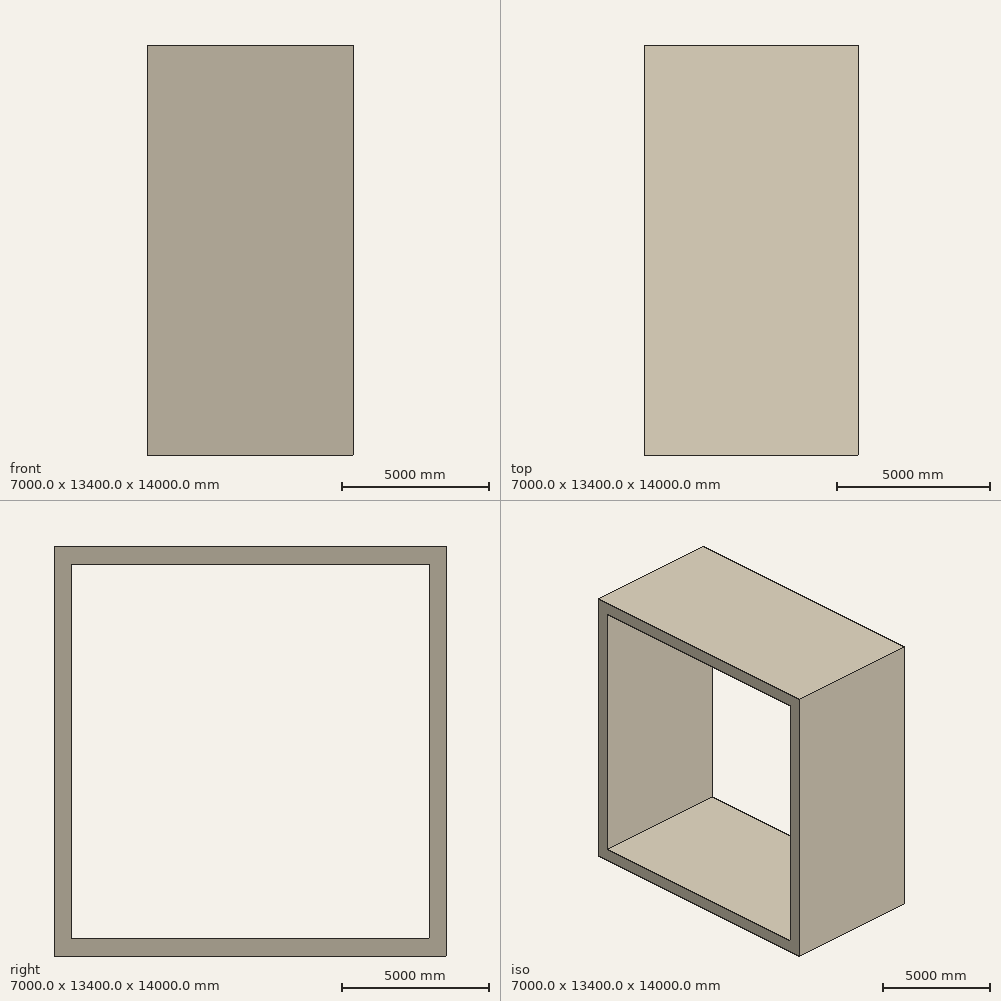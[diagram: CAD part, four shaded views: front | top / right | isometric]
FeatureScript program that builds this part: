
annotation { "Feature Type Name" : "Feature", "Feature Type Description" : "" }
export const myFeature = defineFeature(function(context is Context, id is Id, definition is map)
    precondition{}
    {
        {
            var Q0;
            Q0=qCreatedBy(makeId("Right.planeOp"),FACE);
            var sketch = newSketch(context, id + "F0", { "sketchPlane" : qUnion([Q0])});
            skLineSegment(sketch, "E0.bottom", {"start": v(-6251.52, 6663.35) * mm, "end": v(7148.48, 6663.35) * mm});
            skLineSegment(sketch, "E0.top", {"start": v(-6251.52, -7336.65) * mm, "end": v(7148.48, -7336.65) * mm});
            skLineSegment(sketch, "E0.left", {"start": v(-6251.52, 6663.35) * mm, "end": v(-6251.52, -7336.65) * mm});
            skLineSegment(sketch, "E0.right", {"start": v(7148.48, 6663.35) * mm, "end": v(7148.48, -7336.65) * mm});
            skLineSegment(sketch, "E1.bottom", {"start": v(6548.48, 6063.35) * mm, "end": v(-5651.52, 6063.35) * mm});
            skLineSegment(sketch, "E1.top", {"start": v(6548.48, -6736.65) * mm, "end": v(-5651.52, -6736.65) * mm});
            skLineSegment(sketch, "E1.left", {"start": v(6548.48, 6063.35) * mm, "end": v(6548.48, -6736.65) * mm});
            skLineSegment(sketch, "E1.right", {"start": v(-5651.52, 6063.35) * mm, "end": v(-5651.52, -6736.65) * mm});
            skSolve(sketch);
        }
        {
            var Q0;
            Q0=makeQuery(id+"F0.imprint","IMPRINT",FACE,{"disambiguationData":[TD([[makeQuery(id+"F0.imprint","IMPRINT",EDGE,{"derivedFrom":sQuery(id+"F0.wireOp",EDGE,"E0.bottom")}),-1.0]])]});
            extrude(context, id + "F1", {"entities" : qUnion([Q0]), "oppositeDirection" : true, "depth" : 7000 * mm, "offsetDistance" : 25 * mm});
        }
    });
